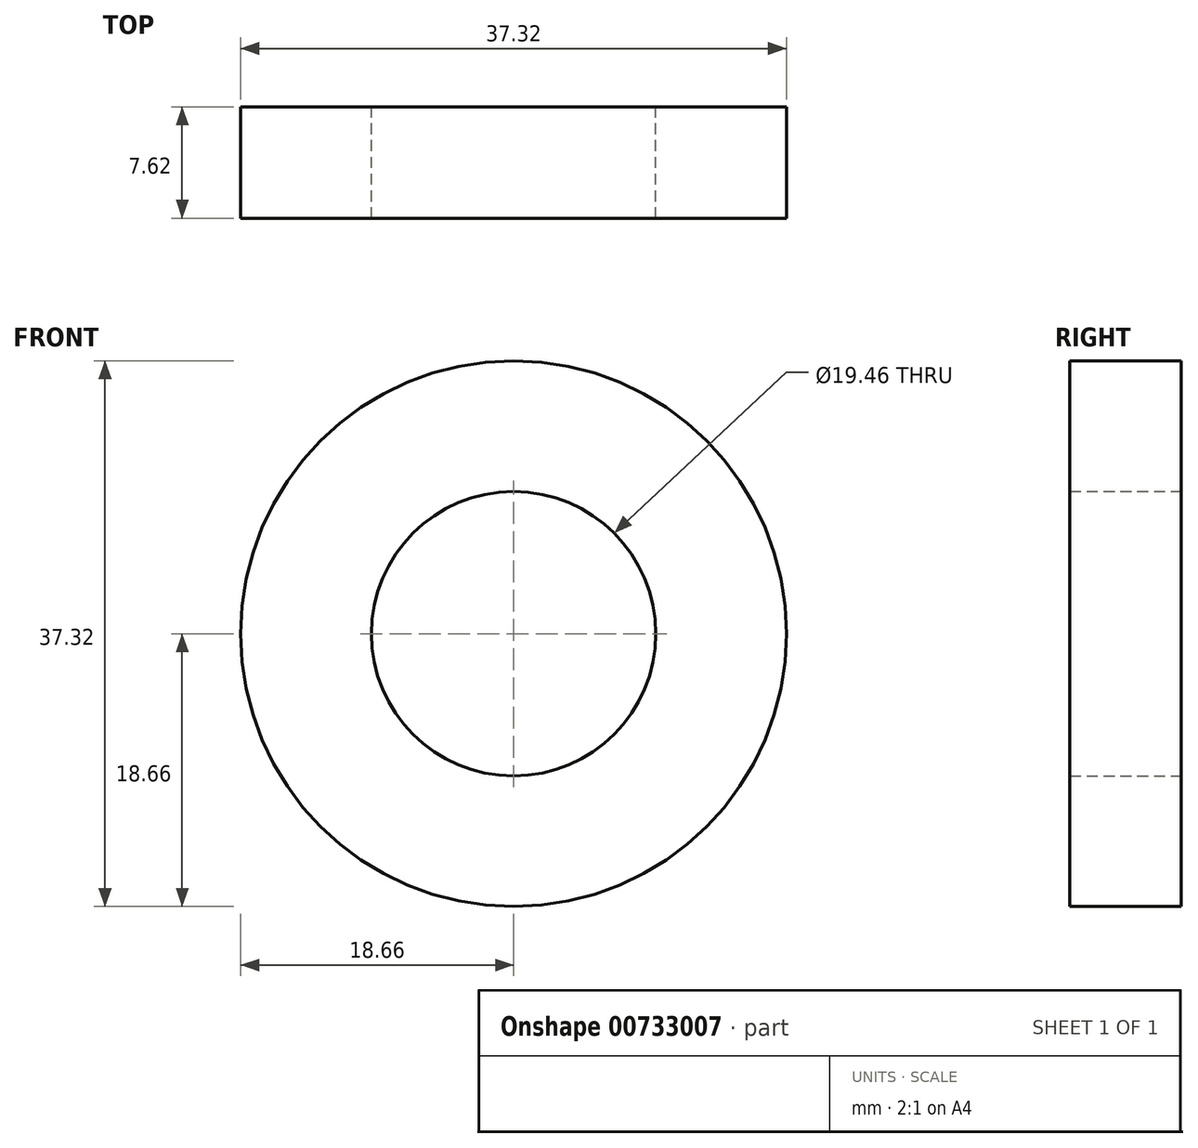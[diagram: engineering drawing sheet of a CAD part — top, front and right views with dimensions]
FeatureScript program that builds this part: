
annotation { "Feature Type Name" : "Feature", "Feature Type Description" : "" }
export const myFeature = defineFeature(function(context is Context, id is Id, definition is map)
    precondition{}
    {
        {
            var Q0;
            Q0=qCreatedBy(makeId("Front.planeOp"),FACE);
            var sketch = newSketch(context, id + "F0", { "sketchPlane" : qUnion([Q0])});
            skPoint(sketch, "E0.middle", {"position": v(0, 0) * mm});
            skCircle(sketch, "E1", {"center": v(0, 0) * mm, "radius": 18.66 * mm});
            skCircle(sketch, "E2", {"center": v(0, 0) * mm, "radius": 9.73 * mm});
            skSolve(sketch);
        }
        {
            var Q0;
            Q0=makeQuery(id+"F0.imprint","IMPRINT",FACE,{"disambiguationData":[TD([[makeQuery(id+"F0.imprint","IMPRINT",EDGE,{"derivedFrom":sQuery(id+"F0.wireOp",EDGE,"E1")}),1.0]])]});
            extrude(context, id + "F1", {"entities" : qUnion([Q0]), "depth" : 7.62 * mm, "offsetDistance" : 25.4 * mm});
        }
    });
